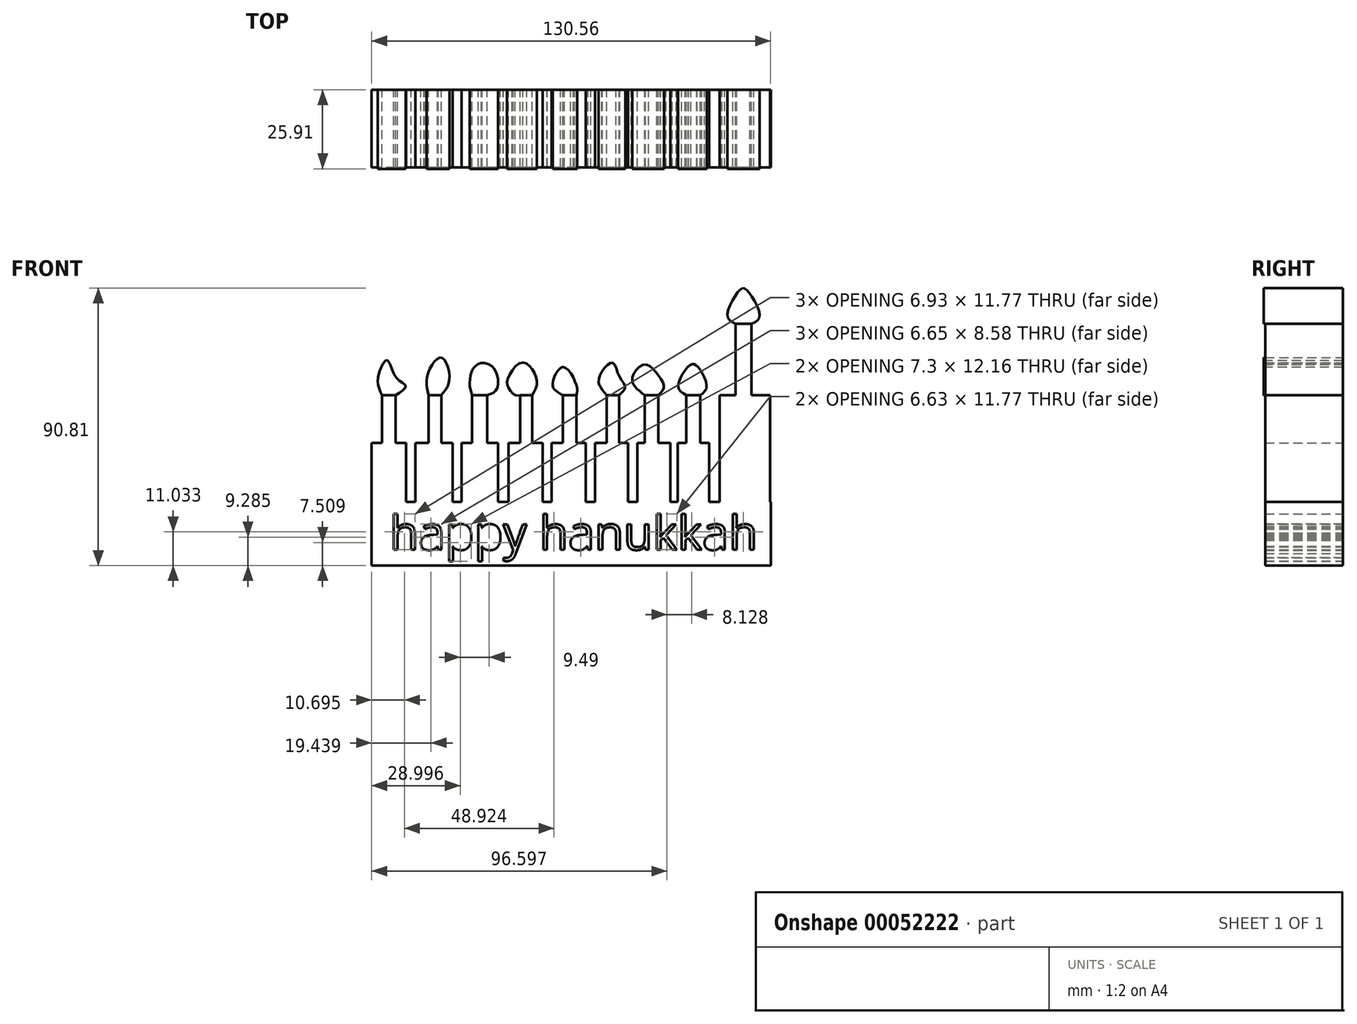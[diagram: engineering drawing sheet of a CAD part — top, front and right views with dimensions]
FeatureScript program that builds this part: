
annotation { "Feature Type Name" : "Feature", "Feature Type Description" : "" }
export const myFeature = defineFeature(function(context is Context, id is Id, definition is map)
    precondition{}
    {
        {
            var Q0;
            Q0=qCreatedBy(makeId("Front.planeOp"),FACE);
            var sketch = newSketch(context, id + "F0", { "sketchPlane" : qUnion([Q0])});
            skLineSegment(sketch, "E0", {"start": v(74.46, -35.01) * mm, "end": v(74.46, 0) * mm});
            skLineSegment(sketch, "E1", {"start": v(74.46, 0) * mm, "end": v(57.91, 0) * mm});
            skLineSegment(sketch, "E2", {"start": v(57.91, 0) * mm, "end": v(57.91, -35.01) * mm});
            skLineSegment(sketch, "E3", {"start": v(54.48, -35.01) * mm, "end": v(54.48, -15.64) * mm});
            skLineSegment(sketch, "E4", {"start": v(54.48, -15.64) * mm, "end": v(44.2, -15.64) * mm});
            skLineSegment(sketch, "E5", {"start": v(44.2, -15.64) * mm, "end": v(44.2, -35.01) * mm});
            skLineSegment(sketch, "E6", {"start": v(41.77, -35.01) * mm, "end": v(41.77, -15.64) * mm});
            skLineSegment(sketch, "E7", {"start": v(41.77, -15.64) * mm, "end": v(31.08, -15.64) * mm});
            skLineSegment(sketch, "E8", {"start": v(31.08, -15.64) * mm, "end": v(31.08, -35.01) * mm});
            skLineSegment(sketch, "E9", {"start": v(28.05, -35.01) * mm, "end": v(28.05, -15.64) * mm});
            skLineSegment(sketch, "E10", {"start": v(28.05, -15.64) * mm, "end": v(17.15, -15.64) * mm});
            skLineSegment(sketch, "E11", {"start": v(17.15, -15.64) * mm, "end": v(17.15, -35.01) * mm});
            skLineSegment(sketch, "E12", {"start": v(14.13, -35.01) * mm, "end": v(14.13, -15.64) * mm});
            skLineSegment(sketch, "E13", {"start": v(14.13, -15.64) * mm, "end": v(3.03, -15.64) * mm});
            skLineSegment(sketch, "E14", {"start": v(3.03, -15.64) * mm, "end": v(3.03, -35.01) * mm});
            skLineSegment(sketch, "E15", {"start": v(0, -35.01) * mm, "end": v(0, -15.64) * mm});
            skLineSegment(sketch, "E16", {"start": v(0, -15.64) * mm, "end": v(-11.1, -15.64) * mm});
            skLineSegment(sketch, "E17", {"start": v(-11.1, -15.64) * mm, "end": v(-11.1, -35.01) * mm});
            skLineSegment(sketch, "E18", {"start": v(-14.53, -35.01) * mm, "end": v(-14.53, -15.64) * mm});
            skLineSegment(sketch, "E19", {"start": v(-14.53, -15.64) * mm, "end": v(-26.43, -15.64) * mm});
            skLineSegment(sketch, "E20", {"start": v(-26.43, -15.64) * mm, "end": v(-26.43, -35.01) * mm});
            skLineSegment(sketch, "E21", {"start": v(-29.46, -35.01) * mm, "end": v(-29.46, -15.64) * mm});
            skLineSegment(sketch, "E22", {"start": v(-29.46, -15.64) * mm, "end": v(-41.57, -15.64) * mm});
            skLineSegment(sketch, "E23", {"start": v(-41.57, -15.64) * mm, "end": v(-41.57, -35.01) * mm});
            skLineSegment(sketch, "E24", {"start": v(-44.6, -35.01) * mm, "end": v(-44.6, -15.64) * mm});
            skLineSegment(sketch, "E25", {"start": v(-44.6, -15.64) * mm, "end": v(-55.9, -15.64) * mm});
            skLineSegment(sketch, "E26", {"start": v(-55.9, -15.64) * mm, "end": v(-55.9, -35.01) * mm});
            skLineSegment(sketch, "E27.bottom", {"start": v(-55.9, -35.01) * mm, "end": v(74.66, -35.01) * mm});
            skLineSegment(sketch, "E27.top", {"start": v(-55.9, -55.8) * mm, "end": v(74.66, -55.8) * mm});
            skLineSegment(sketch, "E27.left", {"start": v(-55.9, -35.01) * mm, "end": v(-55.9, -55.8) * mm});
            skLineSegment(sketch, "E27.right", {"start": v(74.66, -35.01) * mm, "end": v(74.66, -55.8) * mm});
            skLineSegment(sketch, "E28", {"start": v(63.16, 23.3) * mm, "end": v(63.16, 0) * mm});
            skLineSegment(sketch, "E29", {"start": v(63.16, 23.3) * mm, "end": v(68.4, 23.3) * mm});
            skLineSegment(sketch, "E30", {"start": v(68.4, 23.3) * mm, "end": v(68.4, 0) * mm});
            skPoint(sketch, "E31.3.internal.snap0", {"position": v(65.78, 23.3) * mm});
            skFitSpline(sketch, "E31", {"points": [v(68.4, 23.3) * mm, v(71.03, 25.53) * mm, v(68.4, 32.39) * mm, v(65.78, 35.01) * mm, v(63.16, 32.59) * mm, v(60.54, 25.73) * mm, v(63.16, 23.3) * mm], "startDerivative": vector(24.92, 11.17) * mm, "endDerivative": vector(24.53, -12.37) * mm});
            skLineSegment(sketch, "E32", {"start": v(51.66, -15.64) * mm, "end": v(51.66, 0) * mm});
            skLineSegment(sketch, "E33", {"start": v(51.66, 0) * mm, "end": v(47.02, 0) * mm});
            skLineSegment(sketch, "E34", {"start": v(47.02, 0) * mm, "end": v(47.02, -15.64) * mm});
            skLineSegment(sketch, "E35", {"start": v(37.94, -15.64) * mm, "end": v(37.94, 0) * mm});
            skLineSegment(sketch, "E36", {"start": v(37.94, 0) * mm, "end": v(33.5, 0) * mm});
            skLineSegment(sketch, "E37", {"start": v(33.5, 0) * mm, "end": v(33.5, -15.64) * mm});
            skLineSegment(sketch, "E38", {"start": v(25.02, -15.64) * mm, "end": v(25.02, 0) * mm});
            skLineSegment(sketch, "E39", {"start": v(25.02, 0) * mm, "end": v(20.99, 0) * mm});
            skLineSegment(sketch, "E40", {"start": v(20.99, 0) * mm, "end": v(20.99, -15.64) * mm});
            skLineSegment(sketch, "E41", {"start": v(11.1, -15.64) * mm, "end": v(11.1, 0) * mm});
            skLineSegment(sketch, "E42", {"start": v(11.1, 0) * mm, "end": v(6.66, -0.1) * mm});
            skLineSegment(sketch, "E43", {"start": v(6.66, -0.1) * mm, "end": v(6.66, -15.64) * mm});
            skLineSegment(sketch, "E44", {"start": v(-3.43, -15.64) * mm, "end": v(-3.43, 0) * mm});
            skLineSegment(sketch, "E45", {"start": v(-3.43, 0) * mm, "end": v(-7.26, 0) * mm});
            skLineSegment(sketch, "E46", {"start": v(-7.26, 0) * mm, "end": v(-7.26, -15.64) * mm});
            skLineSegment(sketch, "E47", {"start": v(-18.16, -15.64) * mm, "end": v(-18.16, 0) * mm});
            skLineSegment(sketch, "E48", {"start": v(-18.16, 0) * mm, "end": v(-23, 0) * mm});
            skLineSegment(sketch, "E49", {"start": v(-23, 0) * mm, "end": v(-23, -15.64) * mm});
            skLineSegment(sketch, "E50", {"start": v(-33.1, -15.64) * mm, "end": v(-33.1, 0) * mm});
            skLineSegment(sketch, "E51", {"start": v(-33.1, 0) * mm, "end": v(-37.33, 0) * mm});
            skLineSegment(sketch, "E52", {"start": v(-37.33, 0) * mm, "end": v(-37.33, -15.64) * mm});
            skLineSegment(sketch, "E53", {"start": v(-48.03, -15.64) * mm, "end": v(-48.03, 0) * mm});
            skLineSegment(sketch, "E54", {"start": v(-48.03, 0) * mm, "end": v(-52.47, 0) * mm});
            skLineSegment(sketch, "E55", {"start": v(-52.47, 0) * mm, "end": v(-52.47, -15.64) * mm});
            skPoint(sketch, "E56.3.internal.snap0", {"position": v(49.34, 0) * mm});
            skFitSpline(sketch, "E56", {"points": [v(51.66, 0) * mm, v(53.68, 2.52) * mm, v(51.66, 8.17) * mm, v(49.34, 10.2) * mm, v(47.02, 8.58) * mm, v(44.4, 2.52) * mm, v(47.02, 0) * mm], "startDerivative": vector(18.7, 13.91) * mm, "endDerivative": vector(23.2, -12.28) * mm});
            skFitSpline(sketch, "E57", {"points": [v(37.94, 0) * mm, v(39.75, 2.52) * mm, v(37.94, 6.36) * mm, v(33.5, 9.99) * mm, v(29.46, 5.95) * mm, v(30.47, 2.52) * mm, v(33.5, 0) * mm], "startDerivative": vector(18.1, 16.92) * mm, "endDerivative": vector(20.66, -14.59) * mm});
            skFitSpline(sketch, "E58", {"points": [v(25.02, 0) * mm, v(27.04, 2.52) * mm, v(25.02, 6.36) * mm, v(22.8, 10.6) * mm, v(18.77, 6.36) * mm, v(18.77, 2.93) * mm, v(20.99, 0) * mm], "startDerivative": vector(20.33, 16.68) * mm, "endDerivative": vector(16.55, -18.36) * mm});
            skFitSpline(sketch, "E59", {"points": [v(11.1, 0) * mm, v(11.1, 3.13) * mm, v(6.66, 9.18) * mm, v(3.43, 4.34) * mm, v(3.83, 1.92) * mm, v(6.66, -0.1) * mm], "startDerivative": vector(3.52, 14.56) * mm, "endDerivative": vector(18.53, -10.83) * mm});
            skFitSpline(sketch, "E60", {"points": [v(-3.43, 0) * mm, v(-1.82, 3.73) * mm, v(-3.43, 8.58) * mm, v(-7.06, 10.6) * mm, v(-11.3, 5.55) * mm, v(-11.3, 2.72) * mm, v(-9.08, 0) * mm, v(-7.26, 0) * mm], "startDerivative": vector(15.38, 24.09) * mm, "endDerivative": vector(18.35, 4.56) * mm});
            skFitSpline(sketch, "E61", {"points": [v(-18.16, 0) * mm, v(-14.93, 1.92) * mm, v(-15.94, 8.78) * mm, v(-20.38, 10.4) * mm, v(-23, 7.97) * mm, v(-23.81, 3.33) * mm, v(-23, 0) * mm], "startDerivative": vector(25.56, 6.62) * mm, "endDerivative": vector(7.36, -21.25) * mm});
            skFitSpline(sketch, "E62", {"points": [v(-33.1, 0) * mm, v(-30.47, 5.15) * mm, v(-33.1, 12.2) * mm, v(-37.53, 6.96) * mm, v(-37.33, 0) * mm], "startDerivative": vector(15.88, 18) * mm, "endDerivative": vector(5.88, -25.8) * mm});
            skFitSpline(sketch, "E63", {"points": [v(-48.03, 0) * mm, v(-44.8, 2.93) * mm, v(-48.03, 5.95) * mm, v(-50.85, 11.4) * mm, v(-53.88, 5.55) * mm, v(-52.47, 0) * mm], "startDerivative": vector(27.9, 17.66) * mm, "endDerivative": vector(12.52, -23.2) * mm});
            skText(sketch, "E64", { "text": "happy hanukkah", "fontName": "OpenSans-Regular.ttf"});
            const initialGuessF0  = {"E64": [-0.05, -0.05065, 1, 0, 0.01115]};
            skSetInitialGuess(sketch, initialGuessF0);
            skSolve(sketch);
        }
        {
            var Q0;
            {var subQ4=sQuery(id+"F0.wireOp",EDGE,"E9");Q0=makeQuery(id+"F0.imprint","IMPRINT",FACE,{"disambiguationData":[TD([[makeQuery(id+"F0.imprint","IMPRINT",EDGE,{"derivedFrom":subQ4}),1.0]])]});}
            var Q1;
            {var subQ4=sQuery(id+"F0.wireOp",EDGE,"E12");Q1=makeQuery(id+"F0.imprint","IMPRINT",FACE,{"disambiguationData":[TD([[makeQuery(id+"F0.imprint","IMPRINT",EDGE,{"derivedFrom":subQ4}),1.0]])]});}
            var Q2;
            {var subQ5=sQuery(id+"F0.wireOp",EDGE,"E15");Q2=makeQuery(id+"F0.imprint","IMPRINT",FACE,{"disambiguationData":[TD([[makeQuery(id+"F0.imprint","IMPRINT",EDGE,{"derivedFrom":subQ5}),1.0]])]});}
            var Q3;
            {var subQ4=sQuery(id+"F0.wireOp",EDGE,"E18");Q3=makeQuery(id+"F0.imprint","IMPRINT",FACE,{"disambiguationData":[TD([[makeQuery(id+"F0.imprint","IMPRINT",EDGE,{"derivedFrom":subQ4}),1.0]])]});}
            var Q4;
            {var subQ4=sQuery(id+"F0.wireOp",EDGE,"E21");Q4=makeQuery(id+"F0.imprint","IMPRINT",FACE,{"disambiguationData":[TD([[makeQuery(id+"F0.imprint","IMPRINT",EDGE,{"derivedFrom":subQ4}),1.0]])]});}
            var Q5;
            {var subQ4=sQuery(id+"F0.wireOp",EDGE,"E24");Q5=makeQuery(id+"F0.imprint","IMPRINT",FACE,{"disambiguationData":[TD([[makeQuery(id+"F0.imprint","IMPRINT",EDGE,{"derivedFrom":subQ4}),1.0]])]});}
            var Q6;
            Q6=makeQuery(id+"F0.imprint","IMPRINT",FACE,{"disambiguationData":[TD([[makeQuery(id+"F0.imprint","IMPRINT",EDGE,{"derivedFrom":sQuery(id+"F0.wireOp",EDGE,"E27.top")}),1.0]])]});
            var Q7;
            {var subQ4=sQuery(id+"F0.wireOp",EDGE,"E6");Q7=makeQuery(id+"F0.imprint","IMPRINT",FACE,{"disambiguationData":[TD([[makeQuery(id+"F0.imprint","IMPRINT",EDGE,{"derivedFrom":subQ4}),1.0]])]});}
            var Q8;
            {var subQ4=sQuery(id+"F0.wireOp",EDGE,"E3");Q8=makeQuery(id+"F0.imprint","IMPRINT",FACE,{"disambiguationData":[TD([[makeQuery(id+"F0.imprint","IMPRINT",EDGE,{"derivedFrom":subQ4}),1.0]])]});}
            var Q9;
            {var subQ4=sQuery(id+"F0.wireOp",EDGE,"E0");Q9=makeQuery(id+"F0.imprint","IMPRINT",FACE,{"disambiguationData":[TD([[makeQuery(id+"F0.imprint","IMPRINT",EDGE,{"derivedFrom":subQ4}),1.0]])]});}
            var Q10;
            {var subQ0=sQuery(id+"F0.wireOp",EDGE,"E28");Q10=makeQuery(id+"F0.imprint","IMPRINT",FACE,{"disambiguationData":[TD([[makeQuery(id+"F0.imprint","IMPRINT",EDGE,{"derivedFrom":subQ0}),1.0]])]});}
            var Q11;
            {var subQ0=sQuery(id+"F0.wireOp",EDGE,"E32");Q11=makeQuery(id+"F0.imprint","IMPRINT",FACE,{"disambiguationData":[TD([[makeQuery(id+"F0.imprint","IMPRINT",EDGE,{"derivedFrom":subQ0}),1.0]])]});}
            var Q12;
            {var subQ0=sQuery(id+"F0.wireOp",EDGE,"E35");Q12=makeQuery(id+"F0.imprint","IMPRINT",FACE,{"disambiguationData":[TD([[makeQuery(id+"F0.imprint","IMPRINT",EDGE,{"derivedFrom":subQ0}),1.0]])]});}
            var Q13;
            {var subQ0=sQuery(id+"F0.wireOp",EDGE,"E38");Q13=makeQuery(id+"F0.imprint","IMPRINT",FACE,{"disambiguationData":[TD([[makeQuery(id+"F0.imprint","IMPRINT",EDGE,{"derivedFrom":subQ0}),1.0]])]});}
            var Q14;
            {var subQ0=sQuery(id+"F0.wireOp",EDGE,"E41");Q14=makeQuery(id+"F0.imprint","IMPRINT",FACE,{"disambiguationData":[TD([[makeQuery(id+"F0.imprint","IMPRINT",EDGE,{"derivedFrom":subQ0}),1.0]])]});}
            var Q15;
            {var subQ0=sQuery(id+"F0.wireOp",EDGE,"E44");Q15=makeQuery(id+"F0.imprint","IMPRINT",FACE,{"disambiguationData":[TD([[makeQuery(id+"F0.imprint","IMPRINT",EDGE,{"derivedFrom":subQ0}),1.0]])]});}
            var Q16;
            {var subQ0=sQuery(id+"F0.wireOp",EDGE,"E47");Q16=makeQuery(id+"F0.imprint","IMPRINT",FACE,{"disambiguationData":[TD([[makeQuery(id+"F0.imprint","IMPRINT",EDGE,{"derivedFrom":subQ0}),1.0]])]});}
            var Q17;
            {var subQ0=sQuery(id+"F0.wireOp",EDGE,"E50");Q17=makeQuery(id+"F0.imprint","IMPRINT",FACE,{"disambiguationData":[TD([[makeQuery(id+"F0.imprint","IMPRINT",EDGE,{"derivedFrom":subQ0}),1.0]])]});}
            var Q18;
            {var subQ0=sQuery(id+"F0.wireOp",EDGE,"E53");Q18=makeQuery(id+"F0.imprint","IMPRINT",FACE,{"disambiguationData":[TD([[makeQuery(id+"F0.imprint","IMPRINT",EDGE,{"derivedFrom":subQ0}),1.0]])]});}
            extrude(context, id + "F1", {"entities" : qUnion([Q0, Q1, Q2, Q3, Q4, Q5, Q6, Q7, Q8, Q9, Q10, Q11, Q12, Q13, Q14, Q15, Q16, Q17, Q18]), "depth" : 25.4 * mm});
        }
        {
            var Q0;
            Q0=makeQuery(id+"F0.imprint","IMPRINT",FACE,{"disambiguationData":[TD([[makeQuery(id+"F0.imprint","IMPRINT",EDGE,{"derivedFrom":sQuery(id+"F0.wireOp",EDGE,"E54")}),-1.0]])]});
            var Q1;
            Q1=makeQuery(id+"F0.imprint","IMPRINT",FACE,{"disambiguationData":[TD([[makeQuery(id+"F0.imprint","IMPRINT",EDGE,{"derivedFrom":sQuery(id+"F0.wireOp",EDGE,"E51")}),-1.0]])]});
            var Q2;
            Q2=makeQuery(id+"F0.imprint","IMPRINT",FACE,{"disambiguationData":[TD([[makeQuery(id+"F0.imprint","IMPRINT",EDGE,{"derivedFrom":sQuery(id+"F0.wireOp",EDGE,"E48")}),-1.0]])]});
            var Q3;
            Q3=makeQuery(id+"F0.imprint","IMPRINT",FACE,{"disambiguationData":[TD([[makeQuery(id+"F0.imprint","IMPRINT",EDGE,{"derivedFrom":sQuery(id+"F0.wireOp",EDGE,"E45")}),-1.0]])]});
            var Q4;
            Q4=makeQuery(id+"F0.imprint","IMPRINT",FACE,{"disambiguationData":[TD([[makeQuery(id+"F0.imprint","IMPRINT",EDGE,{"derivedFrom":sQuery(id+"F0.wireOp",EDGE,"E42")}),-1.0]])]});
            var Q5;
            Q5=makeQuery(id+"F0.imprint","IMPRINT",FACE,{"disambiguationData":[TD([[makeQuery(id+"F0.imprint","IMPRINT",EDGE,{"derivedFrom":sQuery(id+"F0.wireOp",EDGE,"E39")}),-1.0]])]});
            var Q6;
            Q6=makeQuery(id+"F0.imprint","IMPRINT",FACE,{"disambiguationData":[TD([[makeQuery(id+"F0.imprint","IMPRINT",EDGE,{"derivedFrom":sQuery(id+"F0.wireOp",EDGE,"E36")}),-1.0]])]});
            var Q7;
            Q7=makeQuery(id+"F0.imprint","IMPRINT",FACE,{"disambiguationData":[TD([[makeQuery(id+"F0.imprint","IMPRINT",EDGE,{"derivedFrom":sQuery(id+"F0.wireOp",EDGE,"E33")}),-1.0]])]});
            var Q8;
            Q8=makeQuery(id+"F0.imprint","IMPRINT",FACE,{"disambiguationData":[TD([[makeQuery(id+"F0.imprint","IMPRINT",EDGE,{"derivedFrom":sQuery(id+"F0.wireOp",EDGE,"E29")}),1.0]])]});
            extrude(context, id + "F2", {"entities" : qUnion([Q0, Q1, Q2, Q3, Q4, Q5, Q6, Q7, Q8]), "operationType" : NewBodyOperationType.ADD, "depth" : 25.91 * mm});
        }
    });
